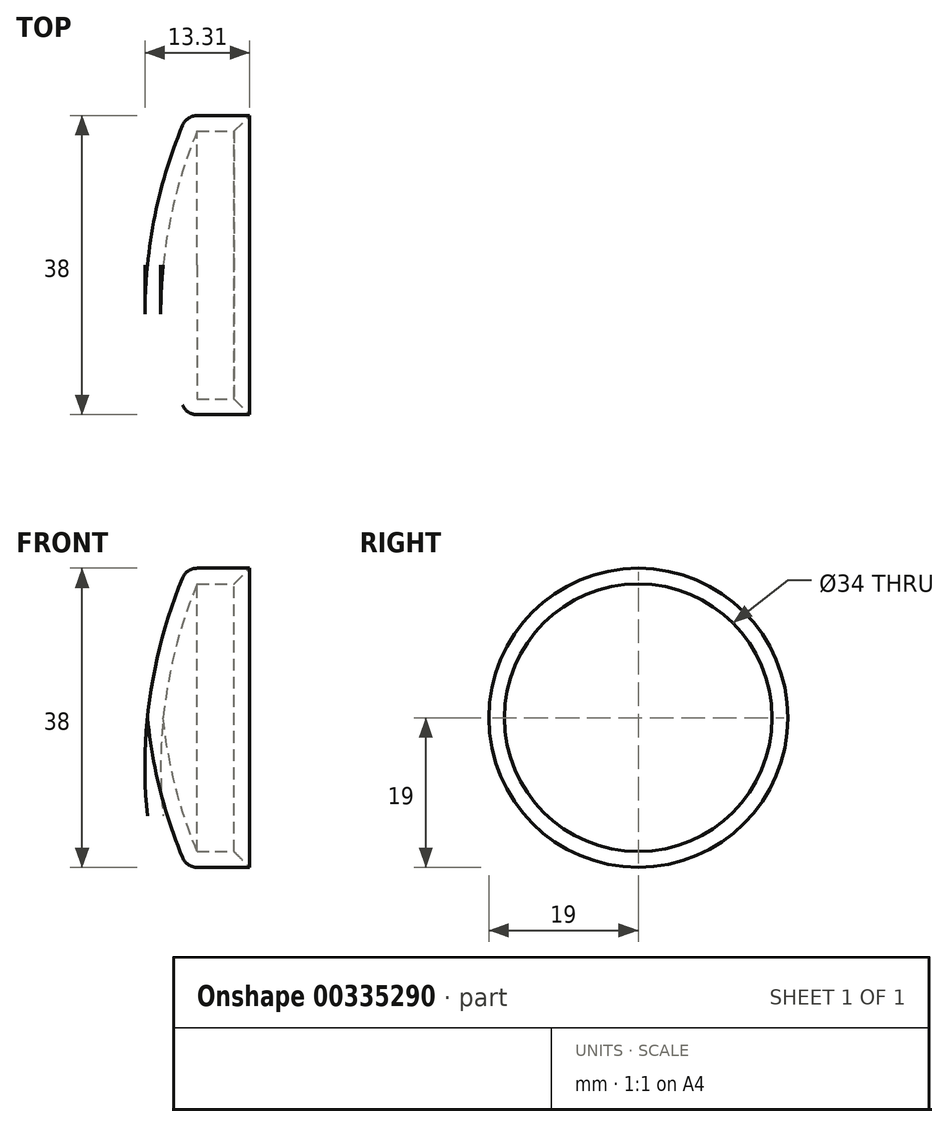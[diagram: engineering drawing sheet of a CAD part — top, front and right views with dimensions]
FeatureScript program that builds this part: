
annotation { "Feature Type Name" : "Feature", "Feature Type Description" : "" }
export const myFeature = defineFeature(function(context is Context, id is Id, definition is map)
    precondition{}
    {
        {
            var Q0;
            Q0=qCreatedBy(makeId("Front.planeOp"),FACE);
            var sketch = newSketch(context, id + "F0", { "sketchPlane" : qUnion([Q0])});
            skLineSegment(sketch, "E0", {"start": v(0, 0) * mm, "end": v(-13, 0) * mm});
            skArc(sketch, "E1", {"start": v(-8, 19) * mm, "mid": v(-11.25, 9.7) * mm, "end": v(-13, 0) * mm});
            skLineSegment(sketch, "E2", {"start": v(0, 19) * mm, "end": v(-8, 19) * mm});
            skArc(sketch, "E3.0", {"start": v(-6.68, 17) * mm, "mid": v(-9.45, 8.66) * mm, "end": v(-10.99, 0) * mm});
            skLineSegment(sketch, "E4.0", {"start": v(0, 17) * mm, "end": v(-6.68, 17) * mm});
            skLineSegment(sketch, "E5", {"start": v(0, 17) * mm, "end": v(0, 19) * mm});
            skSolve(sketch);
        }
        {
            var Q0;
            {var subQ1=sQuery(id+"F0.wireOp",EDGE,"E1");Q0=makeQuery(id+"F0.imprint","IMPRINT",FACE,{"disambiguationData":[TD([[makeQuery(id+"F0.imprint","IMPRINT",EDGE,{"derivedFrom":subQ1}),1.0]])]});}
            var Q1;
            Q1=sQuery(id+"F0.wireOp",EDGE,"E0");
            revolve(context, id + "F1", {"entities" : qUnion([Q0]), "axis" : qUnion([Q1]), "revolveType" : RevolveType.FULL});
        }
        {
            var Q0;
            Q0=makeQuery(id+"F1.opRevolve","SWEPT_EDGE",EDGE,{"disambiguationData":[OSD([sQuery(id+"F0.wireOp",EDGE,"E1"),sQuery(id+"F0.wireOp",EDGE,"E2")])]});
            fillet(context, id + "F2", {"entities" : qUnion([Q0]), "radius" : 2 * mm, "tangentPropagation" : true, "allowEdgeOverflow" : false});
        }
        {
            var Q0;
            Q0=makeQuery(id+"F1.opRevolve","SWEPT_EDGE",EDGE,{"disambiguationData":[OSD([sQuery(id+"F0.wireOp",EDGE,"E4.0"),sQuery(id+"F0.wireOp",EDGE,"E5")])]});
            chamfer(context, id + "F3", {"entities" : qUnion([Q0]), "width" : 2 * mm, "tangentPropagation" : true});
        }
    });
